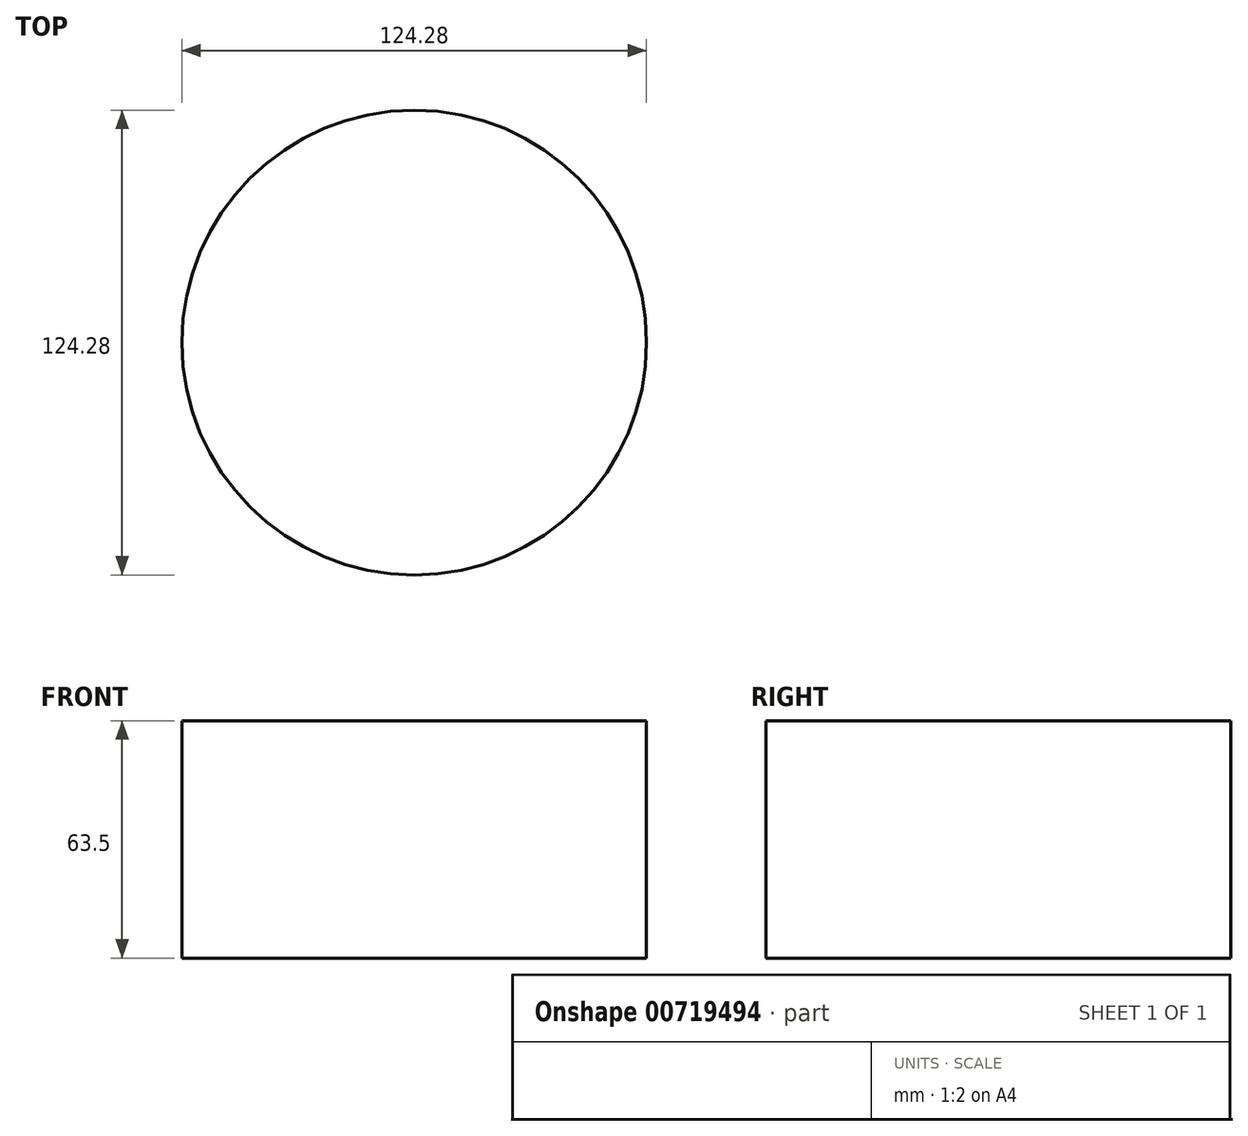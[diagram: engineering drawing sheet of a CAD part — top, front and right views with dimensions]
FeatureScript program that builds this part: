
annotation { "Feature Type Name" : "Feature", "Feature Type Description" : "" }
export const myFeature = defineFeature(function(context is Context, id is Id, definition is map)
    precondition{}
    {
        {
            var Q0;
            Q0=qCreatedBy(makeId("Top.planeOp"),FACE);
            var sketch = newSketch(context, id + "F0", { "sketchPlane" : qUnion([Q0])});
            skCircle(sketch, "E0", {"center": v(0, 0) * mm, "radius": 62.14 * mm});
            skSolve(sketch);
        }
        {
            var Q0;
            Q0=makeQuery(id+"F0.imprint","IMPRINT",FACE,{"disambiguationData":[TD([[makeQuery(id+"F0.imprint","IMPRINT",EDGE,{"derivedFrom":sQuery(id+"F0.wireOp",EDGE,"E0")}),1.0]])]});
            extrude(context, id + "F1", {"entities" : qUnion([Q0]), "endBound" : BoundingType.SYMMETRIC, "depth" : 63.5 * mm, "offsetDistance" : 25.4 * mm});
        }
    });
